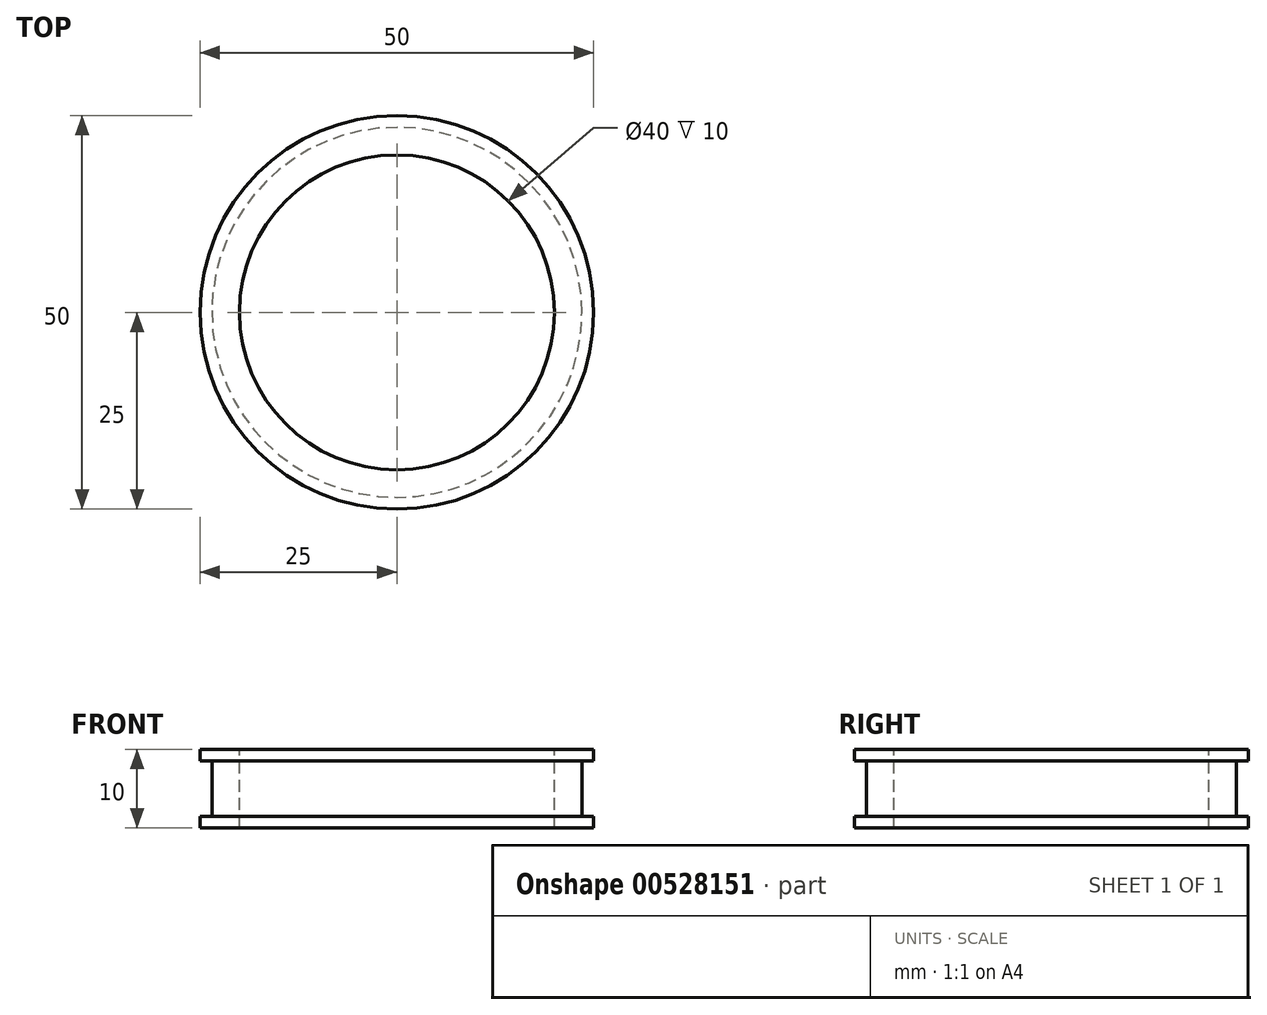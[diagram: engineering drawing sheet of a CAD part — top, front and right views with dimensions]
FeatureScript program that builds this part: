
annotation { "Feature Type Name" : "Feature", "Feature Type Description" : "" }
export const myFeature = defineFeature(function(context is Context, id is Id, definition is map)
    precondition{}
    {
        {
            var Q0;
            Q0=qCreatedBy(makeId("Right.planeOp"),FACE);
            var sketch = newSketch(context, id + "F0", { "sketchPlane" : qUnion([Q0])});
            skLineSegment(sketch, "E0", {"start": v(0, 5) * mm, "end": v(0, -5) * mm});
            skLineSegment(sketch, "E1", {"start": v(0, -5) * mm, "end": v(25, -5) * mm});
            skLineSegment(sketch, "E2", {"start": v(25, -5) * mm, "end": v(25, -3.5) * mm});
            skLineSegment(sketch, "E3", {"start": v(25, -3.5) * mm, "end": v(23.5, -3.5) * mm});
            skLineSegment(sketch, "E4", {"start": v(23.5, -3.5) * mm, "end": v(23.5, 3.5) * mm});
            skLineSegment(sketch, "E5", {"start": v(23.5, 3.5) * mm, "end": v(25, 3.5) * mm});
            skLineSegment(sketch, "E6", {"start": v(25, 3.5) * mm, "end": v(25, 5) * mm});
            skLineSegment(sketch, "E7", {"start": v(25, 5) * mm, "end": v(0, 5) * mm});
            skSolve(sketch);
        }
        {
            var Q0;
            Q0=makeQuery(id+"F0.imprint","IMPRINT",FACE,{"disambiguationData":[TD([[makeQuery(id+"F0.imprint","IMPRINT",EDGE,{"derivedFrom":sQuery(id+"F0.wireOp",EDGE,"E0")}),1.0]])]});
            var Q1;
            Q1=sQuery(id+"F0.wireOp",EDGE,"E0");
            revolve(context, id + "F1", {"entities" : qUnion([Q0]), "axis" : qUnion([Q1]), "revolveType" : RevolveType.FULL});
        }
        {
            var Q0;
            Q0=makeQuery(id+"F1.opRevolve","SWEPT_FACE",FACE,{"disambiguationData":[OSD([sQuery(id+"F0.wireOp",EDGE,"E7")])]});
            var sketch = newSketch(context, id + "F2", { "sketchPlane" : qUnion([Q0])});
            skCircle(sketch, "E8", {"center": v(0, 0) * mm, "radius": 20 * mm});
            skSolve(sketch);
        }
        {
            var Q0;
            Q0 = qSketchRegion(id + "F2", true);
            extrude(context, id + "F3", {"entities" : qUnion([Q0]), "operationType" : NewBodyOperationType.REMOVE, "endBound" : BoundingType.THROUGH_ALL, "oppositeDirection" : true, "depth" : 25 * mm, "offsetDistance" : 25 * mm});
        }
    });
